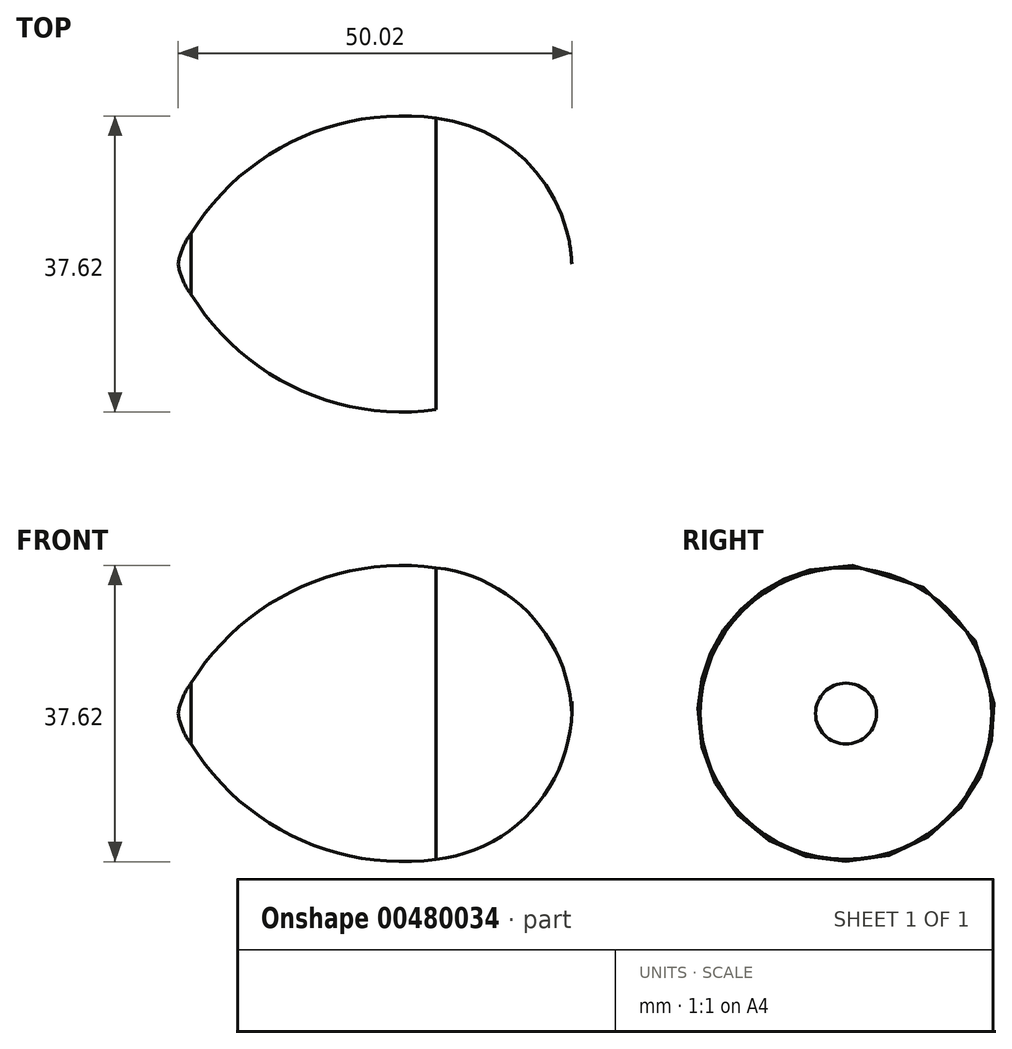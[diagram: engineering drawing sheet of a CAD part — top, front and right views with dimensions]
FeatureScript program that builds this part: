
annotation { "Feature Type Name" : "Feature", "Feature Type Description" : "" }
export const myFeature = defineFeature(function(context is Context, id is Id, definition is map)
    precondition{}
    {
        {
            var Q0;
            Q0=qCreatedBy(makeId("Front.planeOp"),FACE);
            var sketch = newSketch(context, id + "F0", { "sketchPlane" : qUnion([Q0])});
            skLineSegment(sketch, "E0", {"start": v(-28.11, -78.84) * mm, "end": v(-28.11, -71.84) * mm, "construction": true});
            skLineSegment(sketch, "E1", {"start": v(-81.34, -27.34) * mm, "end": v(-31.34, -27.34) * mm});
            skPoint(sketch, "E2.orphan", {"position": v(-94.57, -27.34) * mm});
            skPoint(sketch, "E3.center.orphan", {"position": v(-28.11, -27.34) * mm});
            skPoint(sketch, "E4", {"position": v(46.66, -44.83) * mm});
            skPoint(sketch, "E5", {"position": v(-56.34, -27.34) * mm});
            skLineSegment(sketch, "E6", {"start": v(-48.56, -27.34) * mm, "end": v(-48.56, -8.83) * mm, "construction": true});
            skLineSegment(sketch, "E7", {"start": v(-79.7, -27.34) * mm, "end": v(-79.7, -23.48) * mm, "construction": true});
            skArc(sketch, "E8", {"start": v(-31.34, -27.34) * mm, "mid": v(-36.52, -14.9) * mm, "end": v(-48.56, -8.83) * mm});
            skArc(sketch, "E9", {"start": v(-48.56, -8.83) * mm, "mid": v(-66.3, -11.53) * mm, "end": v(-79.7, -23.48) * mm});
            skArc(sketch, "E10", {"start": v(-79.7, -23.48) * mm, "mid": v(-80.76, -25.3) * mm, "end": v(-81.34, -27.34) * mm});
            skSolve(sketch);
        }
        {
            var Q0;
            Q0=qSketchRegion(id+"F0",true);
            var Q1;
            Q1=sQuery(id+"F0.wireOp",EDGE,"E1");
            revolve(context, id + "F1", {"entities" : qUnion([Q0]), "axis" : qUnion([Q1]), "revolveType" : RevolveType.FULL});
        }
    });
